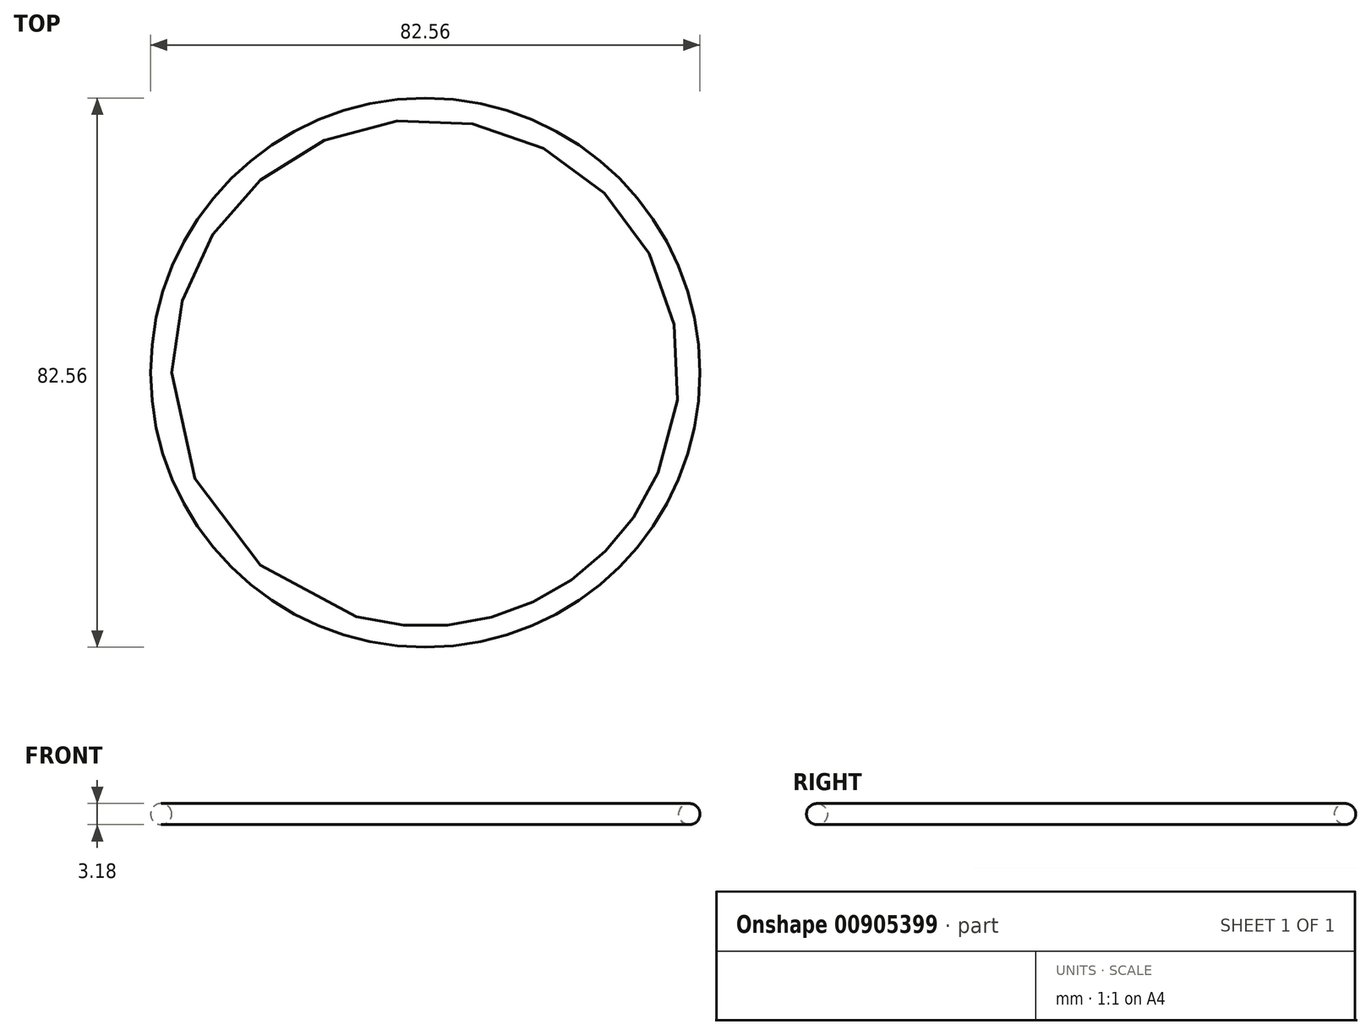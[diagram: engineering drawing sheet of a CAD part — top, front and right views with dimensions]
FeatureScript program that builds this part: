
annotation { "Feature Type Name" : "Feature", "Feature Type Description" : "" }
export const myFeature = defineFeature(function(context is Context, id is Id, definition is map)
    precondition{}
    {
        {
            var Q0;
            Q0=qCreatedBy(makeId("Front.planeOp"),FACE);
            var sketch = newSketch(context, id + "F0", { "sketchPlane" : qUnion([Q0])});
            skLineSegment(sketch, "E0", {"start": v(0, 0) * mm, "end": v(-39.69, 0) * mm, "construction": true});
            skCircle(sketch, "E1", {"center": v(-39.69, 0) * mm, "radius": 1.59 * mm});
            skLineSegment(sketch, "E2", {"start": v(0, 0) * mm, "end": v(0, 30.49) * mm, "construction": true});
            skSolve(sketch);
        }
        {
            var Q0;
            Q0 = qSketchRegion(id + "F0", true);
            var Q1;
            Q1=sQuery(id+"F0.wireOp",EDGE,"E2");
            revolve(context, id + "F1", {"surfaceOperationType" : NewSurfaceOperationType.NEW, "entities" : qUnion([Q0]), "axis" : qUnion([Q1]), "revolveType" : RevolveType.FULL});
        }
    });
